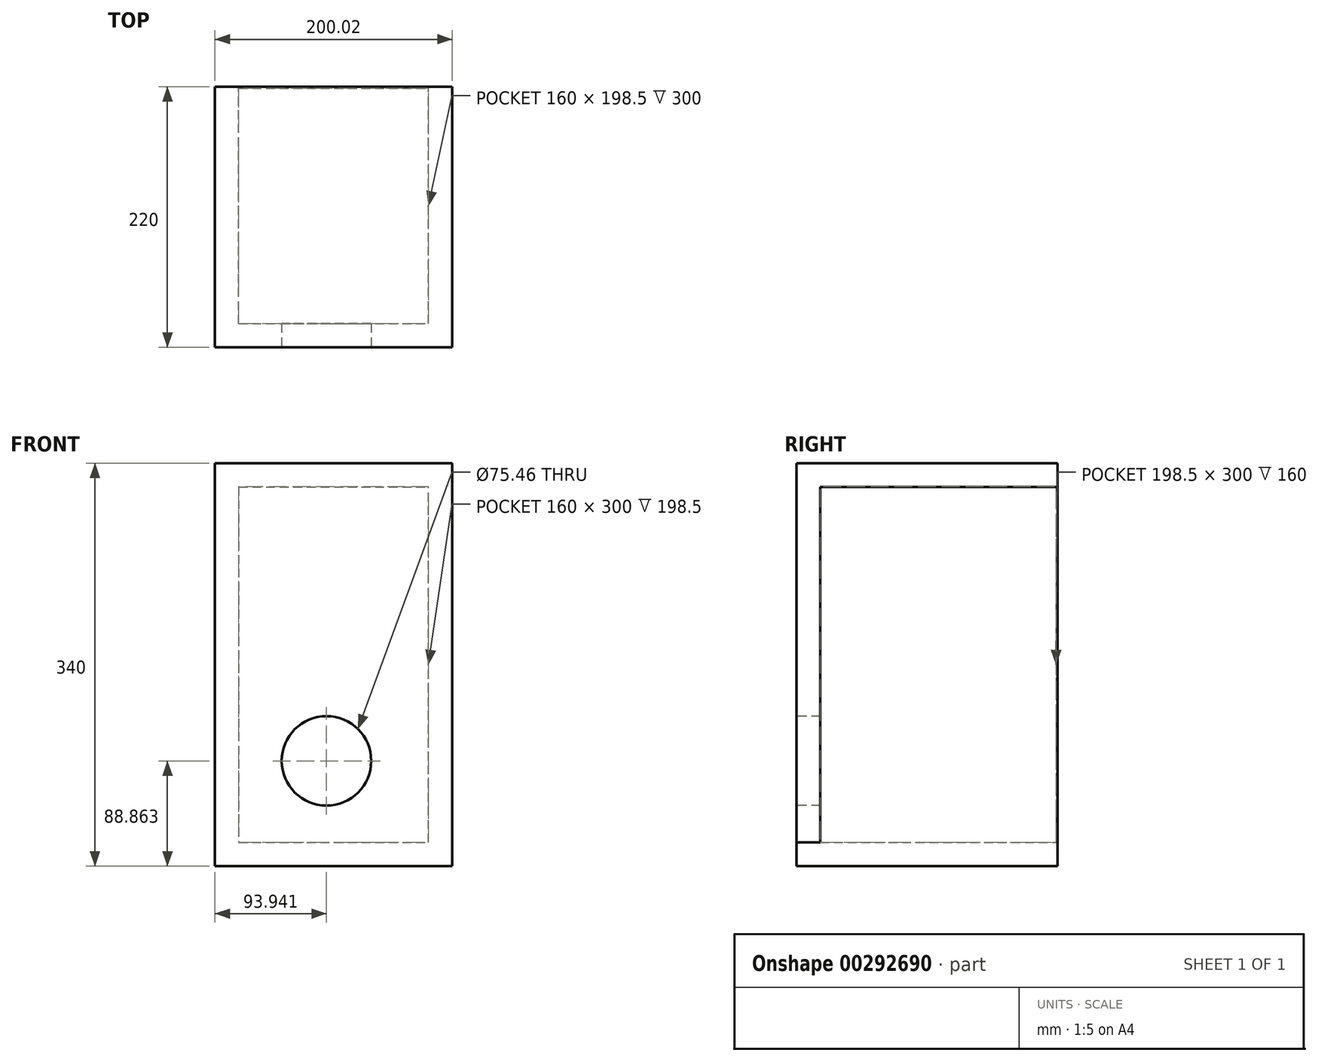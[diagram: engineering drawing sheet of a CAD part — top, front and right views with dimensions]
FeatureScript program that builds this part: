
annotation { "Feature Type Name" : "Feature", "Feature Type Description" : "" }
export const myFeature = defineFeature(function(context is Context, id is Id, definition is map)
    precondition{}
    {
        {
            var Q0;
            Q0=qCreatedBy(makeId("Front.planeOp"),FACE);
            var sketch = newSketch(context, id + "F0", { "sketchPlane" : qUnion([Q0])});
            skLineSegment(sketch, "E0.bottom", {"start": v(0, 0) * mm, "end": v(200, 0) * mm});
            skLineSegment(sketch, "E0.top", {"start": v(0, 300) * mm, "end": v(200, 300) * mm});
            skLineSegment(sketch, "E0.left", {"start": v(0, 0) * mm, "end": v(0, 300) * mm});
            skLineSegment(sketch, "E0.right", {"start": v(200, 0) * mm, "end": v(200, 300) * mm});
            skSolve(sketch);
        }
        {
            var Q0;
            Q0 = qSketchRegion(id + "F0", true);
            extrude(context, id + "F1", {"entities" : qUnion([Q0]), "depth" : 1.5 * mm});
        }
        {
            var Q0;
            Q0=qCreatedBy(makeId("Front.planeOp"),FACE);
            var sketch = newSketch(context, id + "F2", { "sketchPlane" : qUnion([Q0])});
            skLineSegment(sketch, "E1.bottom", {"start": v(0, 0) * mm, "end": v(20, 0) * mm});
            skLineSegment(sketch, "E1.top", {"start": v(0, 300) * mm, "end": v(20, 300) * mm});
            skLineSegment(sketch, "E1.left", {"start": v(0, 0) * mm, "end": v(0, 300) * mm});
            skLineSegment(sketch, "E1.right", {"start": v(20, 0) * mm, "end": v(20, 300) * mm});
            skSolve(sketch);
        }
        {
            var Q0;
            Q0 = qSketchRegion(id + "F2", true);
            extrude(context, id + "F3", {"entities" : qUnion([Q0]), "operationType" : NewBodyOperationType.ADD, "depth" : 200 * mm});
        }
        {
            var Q0;
            Q0=makeQuery(id+"F1.opExtrude","CAP_FACE",FACE,{"disambiguationData":[OSD([sQuery(id+"F0.wireOp",EDGE,"E0.bottom"),sQuery(id+"F0.wireOp",EDGE,"E0.top"),sQuery(id+"F0.wireOp",EDGE,"E0.left"),sQuery(id+"F0.wireOp",EDGE,"E0.right")])],"isStart":false});
            var sketch = newSketch(context, id + "F4", { "sketchPlane" : qUnion([Q0])});
            skLineSegment(sketch, "E2.bottom", {"start": v(200, 0) * mm, "end": v(180, 0) * mm});
            skLineSegment(sketch, "E2.top", {"start": v(200, 300) * mm, "end": v(180, 300) * mm});
            skLineSegment(sketch, "E2.left", {"start": v(200, 0) * mm, "end": v(200, 300) * mm});
            skLineSegment(sketch, "E2.right", {"start": v(180, 0) * mm, "end": v(180, 300) * mm});
            skSolve(sketch);
        }
        {
            var Q0;
            Q0 = qSketchRegion(id + "F4", true);
            extrude(context, id + "F5", {"entities" : qUnion([Q0]), "operationType" : NewBodyOperationType.ADD, "depth" : 200 * mm});
        }
        {
            var Q0;
            Q0=makeQuery(id+"F3.opExtrude","CAP_FACE",FACE,{"disambiguationData":[OSD([sQuery(id+"F2.wireOp",EDGE,"E1.bottom"),sQuery(id+"F2.wireOp",EDGE,"E1.top"),sQuery(id+"F2.wireOp",EDGE,"E1.left"),sQuery(id+"F2.wireOp",EDGE,"E1.right")])],"isStart":false});
            var sketch = newSketch(context, id + "F6", { "sketchPlane" : qUnion([Q0])});
            skLineSegment(sketch, "E3.bottom", {"start": v(0, 300) * mm, "end": v(200.02, 300) * mm});
            skLineSegment(sketch, "E3.top", {"start": v(0, 0) * mm, "end": v(200.02, 0) * mm});
            skLineSegment(sketch, "E3.left", {"start": v(0, 300) * mm, "end": v(0, 0) * mm});
            skLineSegment(sketch, "E3.right", {"start": v(200.02, 300) * mm, "end": v(200.02, 0) * mm});
            skSolve(sketch);
        }
        {
            var Q0;
            Q0 = qSketchRegion(id + "F6", true);
            extrude(context, id + "F7", {"entities" : qUnion([Q0]), "operationType" : NewBodyOperationType.ADD, "depth" : 20 * mm});
        }
        {
            var Q0;
            Q0=makeQuery(id+"F7.boolean.opBoolean","MERGE",FACE,{"derivedFrom":[makeQuery(id+"F5.boolean.opBoolean","MERGE",FACE,{"derivedFrom":[makeQuery(id+"F3.boolean.opBoolean","MERGE",FACE,{"derivedFrom":[makeQuery(id+"F1.opExtrude","SWEPT_FACE",FACE,{"disambiguationData":[OSD([sQuery(id+"F0.wireOp",EDGE,"E0.top")])]}),makeQuery(id+"F3.opExtrude","SWEPT_FACE",FACE,{"disambiguationData":[OSD([sQuery(id+"F2.wireOp",EDGE,"E1.top")])]})]}),makeQuery(id+"F5.opExtrude","SWEPT_FACE",FACE,{"disambiguationData":[OSD([sQuery(id+"F4.wireOp",EDGE,"E2.top")])]})]}),makeQuery(id+"F7.opExtrude","SWEPT_FACE",FACE,{"disambiguationData":[OSD([sQuery(id+"F6.wireOp",EDGE,"E3.bottom")])]})]});
            var sketch = newSketch(context, id + "F8", { "sketchPlane" : qUnion([Q0])});
            skLineSegment(sketch, "E4.bottom", {"start": v(0, 0) * mm, "end": v(200.02, 0) * mm});
            skLineSegment(sketch, "E4.top", {"start": v(0, -220) * mm, "end": v(200.02, -220) * mm});
            skLineSegment(sketch, "E4.left", {"start": v(0, 0) * mm, "end": v(0, -220) * mm});
            skLineSegment(sketch, "E4.right", {"start": v(200.02, 0) * mm, "end": v(200.02, -220) * mm});
            skSolve(sketch);
        }
        {
            var Q0;
            Q0 = qSketchRegion(id + "F8", true);
            extrude(context, id + "F9", {"entities" : qUnion([Q0]), "operationType" : NewBodyOperationType.ADD, "depth" : 20 * mm});
        }
        {
            var Q0;
            Q0=makeQuery(id+"F7.boolean.opBoolean","MERGE",FACE,{"derivedFrom":[makeQuery(id+"F5.boolean.opBoolean","MERGE",FACE,{"derivedFrom":[makeQuery(id+"F3.boolean.opBoolean","MERGE",FACE,{"derivedFrom":[makeQuery(id+"F1.opExtrude","SWEPT_FACE",FACE,{"disambiguationData":[OSD([sQuery(id+"F0.wireOp",EDGE,"E0.bottom")])]}),makeQuery(id+"F3.opExtrude","SWEPT_FACE",FACE,{"disambiguationData":[OSD([sQuery(id+"F2.wireOp",EDGE,"E1.bottom")])]})]}),makeQuery(id+"F5.opExtrude","SWEPT_FACE",FACE,{"disambiguationData":[OSD([sQuery(id+"F4.wireOp",EDGE,"E2.bottom")])]})]}),makeQuery(id+"F7.opExtrude","SWEPT_FACE",FACE,{"disambiguationData":[OSD([sQuery(id+"F6.wireOp",EDGE,"E3.top")])]})]});
            var sketch = newSketch(context, id + "F10", { "sketchPlane" : qUnion([Q0])});
            skLineSegment(sketch, "E5.bottom", {"start": v(0, 220) * mm, "end": v(200, 220) * mm});
            skLineSegment(sketch, "E5.top", {"start": v(0, 0) * mm, "end": v(200, 0) * mm});
            skLineSegment(sketch, "E5.left", {"start": v(0, 220) * mm, "end": v(0, 0) * mm});
            skLineSegment(sketch, "E5.right", {"start": v(200, 220) * mm, "end": v(200, 0) * mm});
            skSolve(sketch);
        }
        {
            var Q0;
            Q0 = qSketchRegion(id + "F10", true);
            var Q1;
            Q1=makeQuery(id+"F9.opExtrude","CAP_FACE",FACE,{"disambiguationData":[OSD([sQuery(id+"F8.wireOp",EDGE,"E4.bottom"),sQuery(id+"F8.wireOp",EDGE,"E4.top"),sQuery(id+"F8.wireOp",EDGE,"E4.left"),sQuery(id+"F8.wireOp",EDGE,"E4.right")])],"isStart":false});
            extrude(context, id + "F11", {"entities" : qUnion([Q0, Q1]), "operationType" : NewBodyOperationType.ADD, "depth" : 20 * mm});
        }
        {
            var Q0;
            Q0=makeQuery(id+"F11.boolean.opBoolean","MERGE",FACE,{"derivedFrom":[makeQuery(id+"F9.boolean.opBoolean","MERGE",FACE,{"derivedFrom":[makeQuery(id+"F7.opExtrude","CAP_FACE",FACE,{"disambiguationData":[OSD([sQuery(id+"F6.wireOp",EDGE,"E3.bottom"),sQuery(id+"F6.wireOp",EDGE,"E3.top"),sQuery(id+"F6.wireOp",EDGE,"E3.left"),sQuery(id+"F6.wireOp",EDGE,"E3.right")])],"isStart":false}),makeQuery(id+"F9.opExtrude","SWEPT_FACE",FACE,{"disambiguationData":[OSD([sQuery(id+"F8.wireOp",EDGE,"E4.top")])]})]}),makeQuery(id+"F11.opExtrude","SWEPT_FACE",FACE,{"disambiguationData":[OSD([sQuery(id+"F10.wireOp",EDGE,"E5.bottom")])]})]});
            var sketch = newSketch(context, id + "F12", { "sketchPlane" : qUnion([Q0])});
            skCircle(sketch, "E6", {"center": v(93.94, 68.86) * mm, "radius": 37.73 * mm});
            skSolve(sketch);
        }
        {
            var Q0;
            Q0=makeQuery(id+"F12.imprint","IMPRINT",FACE,{"disambiguationData":[TD([[makeQuery(id+"F12.imprint","IMPRINT",EDGE,{"derivedFrom":sQuery(id+"F12.wireOp",EDGE,"E6")}),1.0]])]});
            extrude(context, id + "F13", {"entities" : qUnion([Q0]), "operationType" : NewBodyOperationType.REMOVE, "oppositeDirection" : true, "depth" : 92 * mm});
        }
    });
